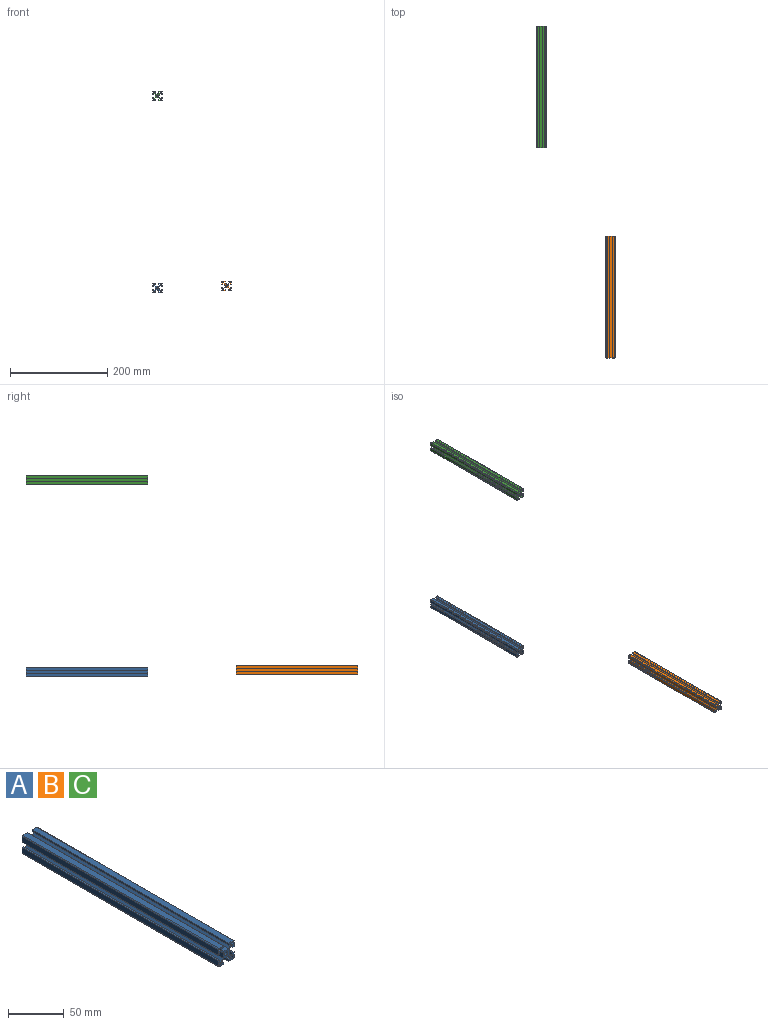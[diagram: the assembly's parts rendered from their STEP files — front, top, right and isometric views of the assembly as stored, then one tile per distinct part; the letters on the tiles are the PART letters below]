
ASSEMBLY  parts=3 mates=2
PART A: 67 faces, bbox 20x250x20 mm
  f0: plane 250x2mm, normal (0,0,-1), area 500mm2, adj f1,f64,f65,f66
  f1: plane 250x2mm, normal (-1,0,0), area 500mm2, adj f0,f2,f65,f66
  f2: plane 250x2mm, normal (0,0,1), area 500mm2, adj f1,f64,f65,f66
  f3: plane 250x2mm, normal (-1,0,0), area 500mm2, adj f4,f59,f65,f66
  f4: plane 250x2mm, normal (0,0,1), area 500mm2, adj f3,f5,f65,f66
  f5: plane 250x2mm, normal (1,0,0), area 500mm2, adj f4,f59,f65,f66
  f6: plane 250x2mm, normal (0,0,1), area 500mm2, adj f7,f60,f65,f66
  f7: plane 250x2mm, normal (1,0,0), area 500mm2, adj f6,f8,f65,f66
  f8: plane 250x2mm, normal (0,0,-1), area 500mm2, adj f7,f60,f65,f66
  f9: cylinder r=1mm len=250mm, axis (0,1,0), area 392.7mm2, adj f10,f62,f65,f66
  f10: plane 250x6mm, normal (1,0,0), area 1500mm2, adj f9,f11,f65,f66
  f11: plane 250x2mm, normal (0,0,1), area 500mm2, adj f10,f12,f65,f66
  f12: plane 250x3mm, normal (-1,0,0), area 750mm2, adj f11,f13,f65,f66
  f13: plane 250x1mm, normal (0,0,1), area 250mm2, adj f12,f14,f65,f66
  f14: plane 250x3mm, normal (0.71,0,0.71), area 1060.7mm2, adj f13,f15,f65,f66
  f15: plane 250x6mm, normal (1,0,0), area 1500mm2, adj f14,f16,f65,f66
  f16: plane 250x3mm, normal (0.71,0,-0.71), area 1060.7mm2, adj f15,f17,f65,f66
  f17: plane 250x1mm, normal (0,0,-1), area 250mm2, adj f16,f18,f65,f66
  f18: plane 250x3mm, normal (-1,0,0), area 750mm2, adj f17,f19,f65,f66
  f19: plane 250x2mm, normal (0,0,-1), area 500mm2, adj f18,f20,f65,f66
  f20: plane 250x6mm, normal (1,0,0), area 1500mm2, adj f19,f21,f65,f66
  f21: cylinder r=1mm len=250mm, axis (0,1,0), area 392.7mm2, adj f20,f22,f65,f66
  f22: plane 250x6mm, normal (0,0,1), area 1500mm2, adj f21,f23,f65,f66
  f23: plane 250x2mm, normal (-1,0,0), area 500mm2, adj f22,f24,f65,f66
  f24: plane 250x3mm, normal (0,0,-1), area 750mm2, adj f23,f25,f65,f66
  f25: plane 250x1mm, normal (-1,0,0), area 250mm2, adj f24,f26,f65,f66
  f26: plane 250x3mm, normal (-0.71,0,0.71), area 1060.7mm2, adj f25,f27,f65,f66
  f27: plane 250x6mm, normal (0,0,1), area 1500mm2, adj f26,f28,f65,f66
  f28: plane 250x3mm, normal (0.71,0,0.71), area 1060.7mm2, adj f27,f29,f65,f66
  f29: plane 250x1mm, normal (1,0,0), area 250mm2, adj f28,f30,f65,f66
  f30: plane 250x3mm, normal (0,0,-1), area 750mm2, adj f29,f31,f65,f66
  f31: plane 250x2mm, normal (1,0,0), area 500mm2, adj f30,f32,f65,f66
  f32: plane 250x6mm, normal (0,0,1), area 1500mm2, adj f31,f33,f65,f66
  f33: cylinder r=1mm len=250mm, axis (0,1,0), area 392.7mm2, adj f32,f34,f65,f66
  f34: plane 250x6mm, normal (-1,0,0), area 1500mm2, adj f33,f35,f65,f66
  f35: plane 250x2mm, normal (0,0,-1), area 500mm2, adj f34,f36,f65,f66
  f36: plane 250x3mm, normal (1,0,0), area 750mm2, adj f35,f37,f65,f66
  f37: plane 250x1mm, normal (0,0,-1), area 250mm2, adj f36,f38,f65,f66
  f38: plane 250x3mm, normal (-0.71,0,-0.71), area 1060.7mm2, adj f37,f39,f65,f66
  f39: plane 250x6mm, normal (-1,0,0), area 1500mm2, adj f38,f40,f65,f66
  f40: plane 250x3mm, normal (-0.71,0,0.71), area 1060.7mm2, adj f39,f41,f65,f66
  f41: plane 250x1mm, normal (0,0,1), area 250mm2, adj f40,f42,f65,f66
  f42: plane 250x3mm, normal (1,0,0), area 750mm2, adj f41,f43,f65,f66
  f43: plane 250x2mm, normal (0,0,1), area 500mm2, adj f42,f44,f65,f66
  f44: plane 250x6mm, normal (-1,0,0), area 1500mm2, adj f43,f45,f65,f66
  f45: cylinder r=1mm len=250mm, axis (0,1,0), area 392.7mm2, adj f44,f46,f65,f66
  f46: plane 250x6mm, normal (0,0,-1), area 1500mm2, adj f45,f47,f65,f66
  f47: plane 250x2mm, normal (1,0,0), area 500mm2, adj f46,f48,f65,f66
  f48: plane 250x3mm, normal (0,0,1), area 750mm2, adj f47,f49,f65,f66
  f49: plane 250x1mm, normal (1,0,0), area 250mm2, adj f48,f50,f65,f66
  f50: plane 250x3mm, normal (0.71,0,-0.71), area 1060.7mm2, adj f49,f51,f65,f66
  f51: plane 250x6mm, normal (0,0,-1), area 1500mm2, adj f50,f52,f65,f66
  f52: plane 250x3mm, normal (-0.71,0,-0.71), area 1060.7mm2, adj f51,f53,f65,f66
  f53: plane 250x1mm, normal (-1,0,0), area 250mm2, adj f52,f54,f65,f66
  f54: plane 250x3mm, normal (0,0,1), area 750mm2, adj f53,f55,f65,f66
  f55: plane 250x2mm, normal (-1,0,0), area 500mm2, adj f54,f62,f65,f66
  f56: plane 250x2mm, normal (0,0,1), area 500mm2, adj f57,f63,f65,f66
  f57: plane 250x2mm, normal (1,0,0), area 500mm2, adj f56,f58,f65,f66
  f58: plane 250x2mm, normal (0,0,-1), area 500mm2, adj f57,f63,f65,f66
  f59: plane 250x2mm, normal (0,0,-1), area 500mm2, adj f3,f5,f65,f66
  f60: plane 250x2mm, normal (-1,0,0), area 500mm2, adj f6,f8,f65,f66
  f61: cylinder r=2.1mm len=250mm, axis (0,1,0), area 3298.7mm2, adj f65,f66
  f62: plane 250x6mm, normal (0,0,-1), area 1500mm2, adj f9,f55,f65,f66
  f63: plane 250x2mm, normal (-1,0,0), area 500mm2, adj f56,f58,f65,f66
  f64: plane 250x2mm, normal (1,0,0), area 500mm2, adj f0,f2,f65,f66
  f65: plane 20x20mm, normal (0,-1,0), area 165.3mm2, adj f0,f1,f2,f3,f4,f5,f6,f7
  f66: plane 20x20mm, normal (0,1,0), area 165.3mm2, adj f0,f1,f2,f3,f4,f5,f6,f7
PART B: same geometry as A
PART C: same geometry as A
PLACE A t=(-67.54,376.68,-109.27)mm
PLACE B t=(74.83,-55.58,-104.75)mm
PLACE C t=(-67.54,376.68,285.95)mm
MATE planar C.f61 <-> A.f61  axis (0,-1,0) through (-67.54,251.68,285.95)mm
MATE planar A.f20 <-> C.f10  axis (1,0,0) through (-57.54,376.68,-103.27)mm
